# Revit family: IS_Contour21Plus_E1536_BIM_GB
name_source: partatom
category: Plumbing Fixtures
units: mm (PartAtom-declared; Revit-internal decimal feet)

## family parameters
Cut with Voids When Loaded = No
Host = Face
OmniClass Number = 23.45.05.21.11.11
OmniClass Title = Water Operated Water Closets
Part Type = Normal
Room Calculation Point = No
Round Connector Dimension = Use Diameter
Shared = Yes

## types (1)
- E1536HY - Contour 21+ Wall hung rimless WC bowl - 700mm projection - hidden fixations - hygenic+ glaze
    Accessories = www.idealspec.co.uk
    AreaUnits = millimeters
    Assembly Code = C1030200
    AssetType = Fixed
    BIMObjectName = IS_IdealStandard_WCPans_Contour21Plus_E1536HY
    Brand = Armitage Shanks
    CWFU = 0
    ConnectionType = Plumbing
    Cost = 0 $
    Default Elevation = 450 mm  [stored 1.47638 ft]
    Description = Contour 21+ 70 cm projection wall mounted rimless WC pan with horizontal outlet and anti-microbial glaze
    DurationUnit = year
    ExpectedLife = 30
    Features = 70 cm projection wall mounted rimless WC pan with horizontal outlet and anti-microbial glaze
    Finish = White
    HWFU = 0
    Help = www.idealspec.co.uk/contact-us.html
    IfcExportAs = IfcSanitaryTerminalType
    IfcExportType = TOILETPAN
    InstallationInstructions = www.idealspec.co.uk/resources.html
    LinearUnits = millimeters
    ManufacturerURL = www.idealspec.co.uk
    Model = E1536HY
    ModelNumber = E1536HY
    ModelReference = Contour 21+ 70 cm projection wall mounted rimless WC pan with horizontal outlet and anti-microbial glaze
    NBSDescription = WC pans
    NBSReference = 45-35-70/384
    Name = WCPans_Contour21Plus_E1536HY_IdealStandard
    NettWeight = 32 Kg
    NominalDepth = 700 mm
    NominalHeight = 365 mm  [stored 1.19751 ft]
    NominalLength = 700 mm
    NominalWidth = 360 mm
    PanColor = White
    PanMaterial = Vitreous china
    PanMounting = BackToWall
    ProductInformation = www.idealspec.co.uk/assets/datasheet/E1536HY
    Shape = Sculptured
    Size = 365 x 700 x 360 mm
    Space = Internal
    SpareParts = www.fastpart-spares.co.uk
    SpilloverLevel = 365 mm  [stored 1.19751 ft]
    ToiletPanType = WashDown
    ToiletType = Other
    URL = www.idealspec.co.uk
    Uniclass2015Code = Pr_40_20_93_94
    Uniclass2015Title = WC pans
    Uniclass2015Version = Products v1.20
    Version = 1
    VolumeUnits = Litres
    WFU = 0
    WarrantyDescription = Manufacturers Warranty
    WarrantyDurationParts = 99
    WarrantyDurationUnit = year

note: [stored X ft] marks values corroborated as IEEE doubles in the binary element streams (Revit-internal decimal feet)

## geometry (parser evidence)
native form markers: Sweep x2
no freeform markers — native parametric forms only
